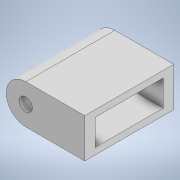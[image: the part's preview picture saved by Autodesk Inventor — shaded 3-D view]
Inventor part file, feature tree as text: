
AUTODESK INVENTOR PART (.ipt)
format: ipt  version: 2022 (Build 260153000, 153)  size: 130,048 bytes
history: native  units: mm
features: extrude x3, sketch x3, other x1, fillet x1
ambient origin geometry x8: Origin, YZ Plane, XZ Plane, XY Plane, X Axis, Y Axis, Z Axis, Center Point
bodies: Solid1 (feature_tree)
feature tree (8):
  extrude  "Extrusion1"  Depth=30.0mm
  extrude  "Extrusion2"  Depth=10.0mm
  extrude  "Extrusion3"  Depth=15.0mm
  other  "Full Round Fillet1"
  fillet  "Fillet1"  Radius=68.0mm
  sketch  "Sketch1"  dims[d0=60.0mm d1=30.0mm]
  sketch  "Sketch2"  dims[d2=68.0mm d3=0.0mm d4=10.0mm]
  sketch  "Sketch3"  dims[d5=15.0mm d6=15.0mm d7=68.0mm d8=0.0mm d9=52.0mm d10=20.0mm d11=34.0mm d12=15.0mm d13=52.0mm d14=0.0mm d15=15.0mm]
